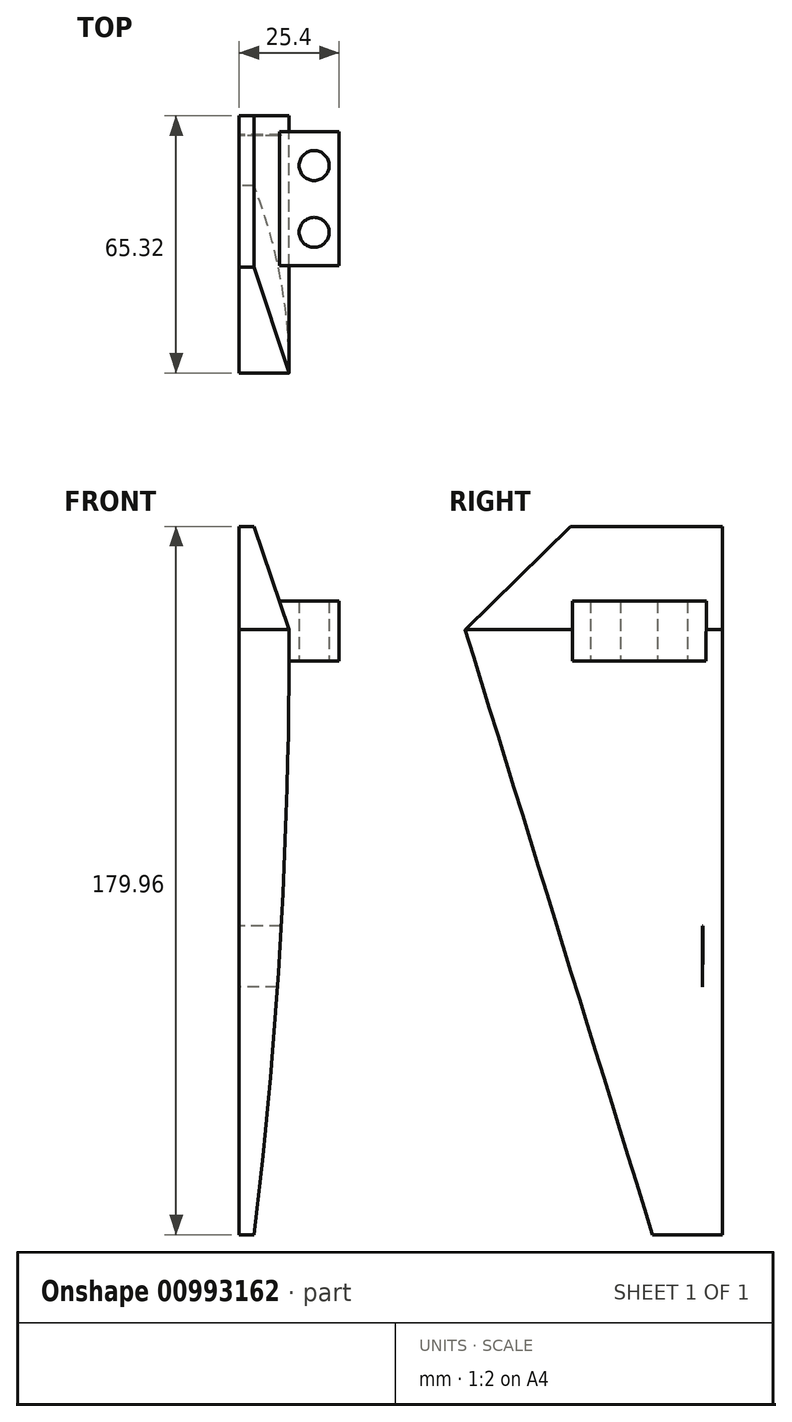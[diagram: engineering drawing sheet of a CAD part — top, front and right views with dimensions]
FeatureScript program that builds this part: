
annotation { "Feature Type Name" : "Feature", "Feature Type Description" : "" }
export const myFeature = defineFeature(function(context is Context, id is Id, definition is map)
    precondition{}
    {
        {
            var Q0;
            Q0=qCreatedBy(makeId("Right.planeOp"),FACE);
            var sketch = newSketch(context, id + "F0", { "sketchPlane" : qUnion([Q0])});
            skLineSegment(sketch, "E0.bottom", {"start": v(-38.02, 66.53) * mm, "end": v(0.08, 66.13) * mm});
            skLineSegment(sketch, "E0.right", {"start": v(0.08, 66.13) * mm, "end": v(0.08, -35.42) * mm});
            skLineSegment(sketch, "E1", {"start": v(-38.02, 66.53) * mm, "end": v(-65.24, 39.87) * mm});
            skLineSegment(sketch, "E2", {"start": v(-3.73, 66.17) * mm, "end": v(-4.94, -50.83) * mm});
            skLineSegment(sketch, "E3.bottom", {"start": v(0.08, -35.42) * mm, "end": v(-4.94, -35.42) * mm});
            skLineSegment(sketch, "E3.top", {"start": v(0.08, -113.83) * mm, "end": v(-4.94, -113.83) * mm});
            skLineSegment(sketch, "E3.left", {"start": v(0.08, -35.42) * mm, "end": v(0.08, -113.83) * mm});
            skLineSegment(sketch, "E3.right", {"start": v(-4.94, -35.42) * mm, "end": v(-4.94, -113.83) * mm});
            skLineSegment(sketch, "E4.bottom", {"start": v(-38.02, 47.16) * mm, "end": v(0.08, 47.16) * mm});
            skLineSegment(sketch, "E4.top", {"start": v(-38.02, 31.92) * mm, "end": v(0.08, 31.92) * mm});
            skLineSegment(sketch, "E4.left", {"start": v(-38.02, 47.16) * mm, "end": v(-38.02, 31.92) * mm});
            skLineSegment(sketch, "E4.right", {"start": v(0.08, 47.16) * mm, "end": v(0.08, 31.92) * mm});
            skPoint(sketch, "E4.middle", {"position": v(-18.97, 39.54) * mm});
            skPoint(sketch, "E4.middle.positionSnap0", {"position": v(-18.97, 66.33) * mm});
            skPoint(sketch, "E4.centerSnap0", {"position": v(-18.97, 66.33) * mm});
            skLineSegment(sketch, "E5", {"start": v(-4.94, -113.83) * mm, "end": v(-17.64, -113.83) * mm});
            skLineSegment(sketch, "E6", {"start": v(-65.24, 39.87) * mm, "end": v(-17.64, -113.83) * mm});
            skSolve(sketch);
        }
        {
            var Q0;
            {var subQ10=sQuery(id+"F0.wireOp",EDGE,"E1");Q0=makeQuery(id+"F0.imprint","IMPRINT",FACE,{"disambiguationData":[TD([[makeQuery(id+"F0.imprint","IMPRINT",EDGE,{"derivedFrom":subQ10}),1.0]])]});}
            var Q1;
            {var subQ3=sQuery(id+"F0.wireOp",EDGE,"E4.top");var subQ5=sQuery(id+"F0.wireOp",EDGE,"E2");var subQ6=makeQuery(id+"F0.imprint","INTERSECT",VERTEX,{"derivedFrom":[subQ5,subQ3]});Q1=makeQuery(id+"F0.imprint","IMPRINT",FACE,{"disambiguationData":[TD([[makeQuery(id+"F0.imprint","IMPRINT",EDGE,{"disambiguationData":[TD([[subQ6,-1.0]])],"derivedFrom":subQ5}),1.0]])]});}
            var Q2;
            {var subQ0=sQuery(id+"F0.wireOp",EDGE,"E3.top");Q2=makeQuery(id+"F0.imprint","IMPRINT",FACE,{"disambiguationData":[TD([[makeQuery(id+"F0.imprint","IMPRINT",EDGE,{"derivedFrom":subQ0}),-1.0]])]});}
            var Q3;
            {var subQ0=sQuery(id+"F0.wireOp",EDGE,"E0.right");var subQ1=sQuery(id+"F0.wireOp",EDGE,"E0.bottom");var subQ2=makeQuery(id+"F0.imprint","INTERSECT",VERTEX,{"derivedFrom":[subQ1,subQ0]});Q3=makeQuery(id+"F0.imprint","IMPRINT",FACE,{"disambiguationData":[TD([[makeQuery(id+"F0.imprint","IMPRINT",EDGE,{"disambiguationData":[TD([[subQ2,1.0]])],"derivedFrom":subQ1}),-1.0]])]});}
            var Q4;
            {var subQ0=sQuery(id+"F0.wireOp",EDGE,"E4.bottom");var subQ1=sQuery(id+"F0.wireOp",EDGE,"E0.right");var subQ2=makeQuery(id+"F0.imprint","INTERSECT",VERTEX,{"derivedFrom":[subQ1,subQ0]});Q4=makeQuery(id+"F0.imprint","IMPRINT",FACE,{"disambiguationData":[TD([[makeQuery(id+"F0.imprint","IMPRINT",EDGE,{"disambiguationData":[TD([[subQ2,-1.0]])],"derivedFrom":subQ1}),-1.0]])]});}
            extrude(context, id + "F1", {"entities" : qUnion([Q0, Q1, Q2, Q3, Q4]), "depth" : 25.4 * mm, "offsetDistance" : 25.4 * mm});
        }
        {
            var Q0;
            Q0=makeQuery(id+"F1.opExtrude","SWEPT_FACE",FACE,{"disambiguationData":[OSD([sQuery(id+"F0.wireOp",EDGE,"E0.right"),sQuery(id+"F0.wireOp",EDGE,"E3.left")])]});
            var sketch = newSketch(context, id + "F2", { "sketchPlane" : qUnion([Q0])});
            skLineSegment(sketch, "E7.top", {"start": v(0, 66.13) * mm, "end": v(-12.7, 66.13) * mm});
            skLineSegment(sketch, "E7.left", {"start": v(0, 39.9) * mm, "end": v(0, 66.13) * mm});
            skLineSegment(sketch, "E7.right", {"start": v(-12.7, 39.9) * mm, "end": v(-12.7, 66.13) * mm});
            skLineSegment(sketch, "E8", {"start": v(-12.7, 39.9) * mm, "end": v(-3.81, 66.13) * mm});
            skLineSegment(sketch, "E9", {"start": v(-25.4, 39.9) * mm, "end": v(-3.81, 66.13) * mm});
            skLineSegment(sketch, "E10", {"start": v(-25.4, 39.9) * mm, "end": v(-12.7, 39.9) * mm});
            skArc(sketch, "E11", {"start": v(-25.4, 39.9) * mm, "mid": v(-22.17, -37.22) * mm, "end": v(-12.7, -113.83) * mm});
            skArc(sketch, "E12", {"start": v(-12.7, 39.9) * mm, "mid": v(-10.57, -37.1) * mm, "end": v(-3.8, -113.83) * mm});
            skSolve(sketch);
        }
        {
            var Q0;
            {var subQ5=sQuery(id+"F0.wireOp",EDGE,"E4.left");Q0=makeQuery(id+"F0.imprint","IMPRINT",FACE,{"disambiguationData":[TD([[makeQuery(id+"F0.imprint","IMPRINT",EDGE,{"derivedFrom":subQ5}),1.0]])]});}
            extrude(context, id + "F3", {"entities" : qUnion([Q0]), "operationType" : NewBodyOperationType.ADD, "depth" : 25.4 * mm, "offsetDistance" : 25.4 * mm});
        }
        {
            var Q0;
            {var subQ0=sQuery(id+"F2.wireOp",EDGE,"E7.right");var subQ3=sQuery(id+"F2.wireOp",EDGE,"E9");var subQ5=makeQuery(id+"F2.imprint","INTERSECT",VERTEX,{"derivedFrom":[subQ0,subQ3]});Q0=makeQuery(id+"F2.imprint","IMPRINT",FACE,{"disambiguationData":[TD([[makeQuery(id+"F2.imprint","IMPRINT",EDGE,{"disambiguationData":[TD([[subQ5,-1.0]])],"derivedFrom":subQ3}),1.0]])]});}
            var Q1;
            {var subQ0=sQuery(id+"F2.wireOp",EDGE,"E11");Q1=makeQuery(id+"F2.imprint","IMPRINT",FACE,{"disambiguationData":[TD([[makeQuery(id+"F2.imprint","IMPRINT",EDGE,{"derivedFrom":subQ0}),-1.0]])]});}
            var Q2;
            {var subQ0=sQuery(id+"F2.wireOp",EDGE,"E7.right");var subQ4=sQuery(id+"F2.wireOp",EDGE,"E9");var subQ5=makeQuery(id+"F2.imprint","INTERSECT",VERTEX,{"derivedFrom":[subQ0,subQ4]});Q2=makeQuery(id+"F2.imprint","IMPRINT",FACE,{"disambiguationData":[TD([[makeQuery(id+"F2.imprint","IMPRINT",EDGE,{"disambiguationData":[TD([[subQ5,-1.0]])],"derivedFrom":subQ0}),1.0]])]});}
            var Q3;
            Q3=makeQuery(id+"F1.opExtrude","SWEPT_FACE",FACE,{"disambiguationData":[OSD([sQuery(id+"F0.wireOp",EDGE,"E0.bottom")])]});
            var Q4;
            {var subQ0=sQuery(id+"F2.wireOp",EDGE,"E8");Q4=makeQuery(id+"F2.imprint","IMPRINT",FACE,{"disambiguationData":[TD([[makeQuery(id+"F2.imprint","IMPRINT",EDGE,{"derivedFrom":subQ0}),1.0]])]});}
            var Q5;
            {var subQ0=sQuery(id+"F2.wireOp",EDGE,"E10");Q5=makeQuery(id+"F2.imprint","IMPRINT",FACE,{"disambiguationData":[TD([[makeQuery(id+"F2.imprint","IMPRINT",EDGE,{"derivedFrom":subQ0}),1.0]])]});}
            var Q6;
            Q6=makeQuery(id+"F2.imprint","IMPRINT",FACE,{"disambiguationData":[TD([[makeQuery(id+"F2.imprint","IMPRINT",EDGE,{"derivedFrom":sQuery(id+"F2.wireOp",EDGE,"E10")}),-1.0]])]});
            extrude(context, id + "F4", {"entities" : qUnion([Q0, Q1, Q2, Q3, Q4, Q5, Q6]), "operationType" : NewBodyOperationType.REMOVE, "oppositeDirection" : true, "depth" : 76.2 * mm, "offsetDistance" : 25.4 * mm});
        }
        {
            var Q0;
            {var subQ5=sQuery(id+"F0.wireOp",EDGE,"E4.left");Q0=makeQuery(id+"F0.imprint","IMPRINT",FACE,{"disambiguationData":[TD([[makeQuery(id+"F0.imprint","IMPRINT",EDGE,{"derivedFrom":subQ5}),1.0]])]});}
            extrude(context, id + "F5", {"entities" : qUnion([Q0]), "operationType" : NewBodyOperationType.ADD, "depth" : 25.4 * mm, "offsetDistance" : 25.4 * mm});
        }
        {
            var Q0;
            Q0=makeQuery(id+"F5.opExtrude","SWEPT_FACE",FACE,{"disambiguationData":[OSD([sQuery(id+"F0.wireOp",EDGE,"E4.top")])]});
            var sketch = newSketch(context, id + "F6", { "sketchPlane" : qUnion([Q0])});
            skCircle(sketch, "E13", {"center": v(19.05, 29.54) * mm, "radius": 3.81 * mm});
            skPoint(sketch, "E13.centerSnap0", {"position": v(19.05, 38.02) * mm});
            skCircle(sketch, "E14", {"center": v(19.05, 12.57) * mm, "radius": 3.81 * mm});
            skPoint(sketch, "E14.centerSnap0", {"position": v(19.05, 4.09) * mm});
            skSolve(sketch);
        }
        {
            var Q0;
            Q0=makeQuery(id+"F6.imprint","IMPRINT",FACE,{"disambiguationData":[TD([[makeQuery(id+"F6.imprint","IMPRINT",EDGE,{"derivedFrom":sQuery(id+"F6.wireOp",EDGE,"E14")}),1.0]])]});
            var Q1;
            Q1=makeQuery(id+"F6.imprint","IMPRINT",FACE,{"disambiguationData":[TD([[makeQuery(id+"F6.imprint","IMPRINT",EDGE,{"derivedFrom":sQuery(id+"F6.wireOp",EDGE,"E13")}),1.0]])]});
            extrude(context, id + "F7", {"entities" : qUnion([Q0, Q1]), "operationType" : NewBodyOperationType.REMOVE, "oppositeDirection" : true, "depth" : 25.4 * mm, "offsetDistance" : 25.4 * mm});
        }
    });
